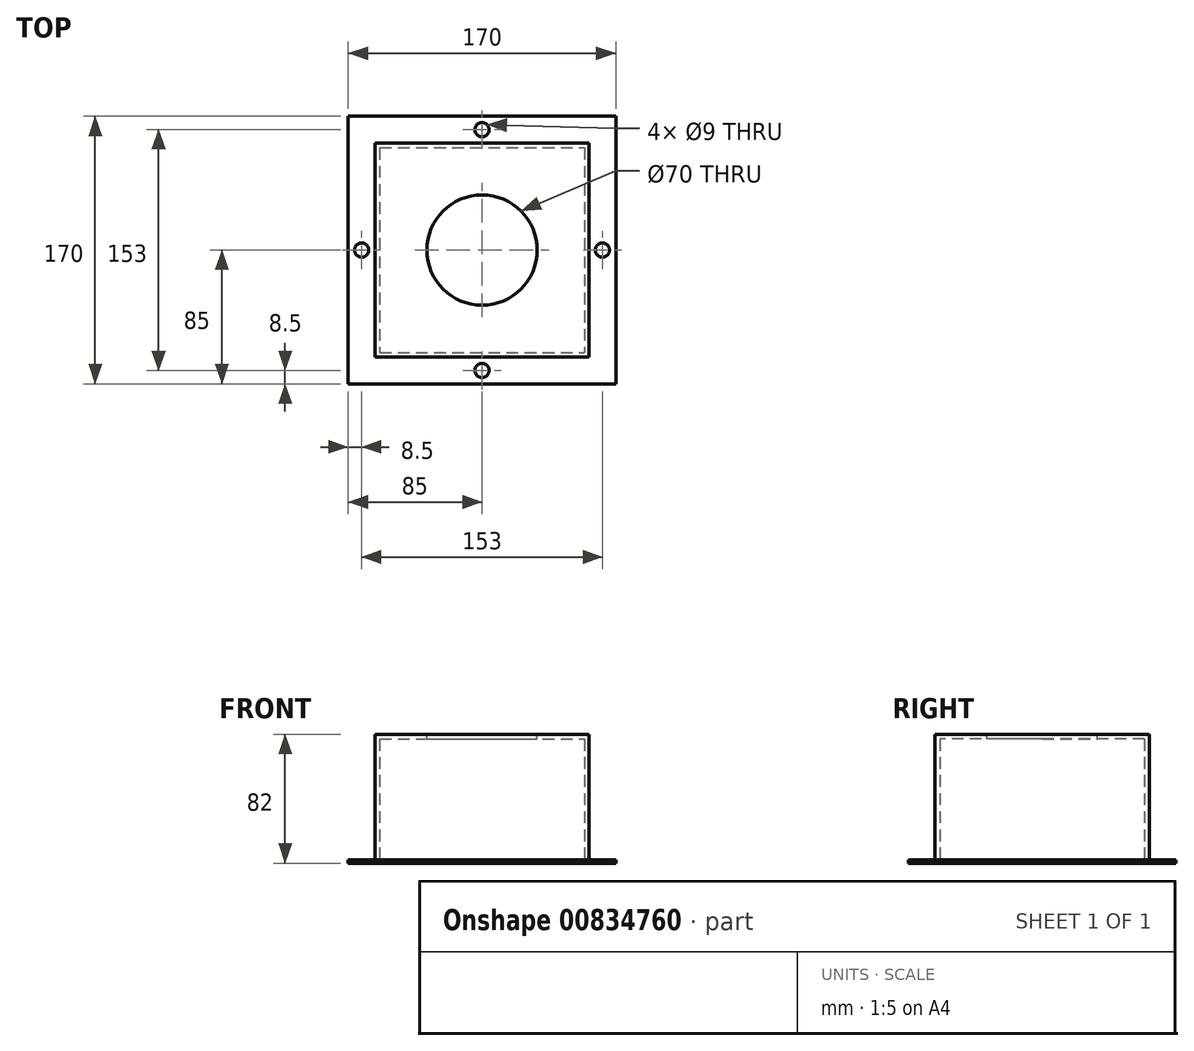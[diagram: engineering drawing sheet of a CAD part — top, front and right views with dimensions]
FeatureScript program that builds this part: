
annotation { "Feature Type Name" : "Feature", "Feature Type Description" : "" }
export const myFeature = defineFeature(function(context is Context, id is Id, definition is map)
    precondition{}
    {
        {
            var Q0;
            Q0=qCreatedBy(makeId("Top.planeOp"),FACE);
            var sketch = newSketch(context, id + "F0", { "sketchPlane" : qUnion([Q0])});
            skLineSegment(sketch, "E0", {"start": v(-85, 85) * mm, "end": v(85, 85) * mm});
            skLineSegment(sketch, "E1", {"start": v(85, 85) * mm, "end": v(85, -85) * mm});
            skLineSegment(sketch, "E2", {"start": v(85, -85) * mm, "end": v(-85, -85) * mm});
            skLineSegment(sketch, "E3", {"start": v(-85, -85) * mm, "end": v(-85, 85) * mm});
            skPoint(sketch, "E4", {"position": v(0, 0) * mm});
            skPoint(sketch, "E4.positionSnap0", {"position": v(-85, 0) * mm});
            skPoint(sketch, "E4.positionSnap1", {"position": v(0, 85) * mm});
            skLineSegment(sketch, "E5.bottom", {"start": v(-65, 65) * mm, "end": v(65, 65) * mm});
            skLineSegment(sketch, "E5.top", {"start": v(-65, -65) * mm, "end": v(65, -65) * mm});
            skLineSegment(sketch, "E5.left", {"start": v(-65, 65) * mm, "end": v(-65, -65) * mm});
            skLineSegment(sketch, "E5.right", {"start": v(65, 65) * mm, "end": v(65, -65) * mm});
            skSolve(sketch);
        }
        {
            var Q0;
            Q0=makeQuery(id+"F0.imprint","IMPRINT",FACE,{"disambiguationData":[TD([[makeQuery(id+"F0.imprint","IMPRINT",EDGE,{"derivedFrom":sQuery(id+"F0.wireOp",EDGE,"E0")}),-1.0]])]});
            extrude(context, id + "F1", {"entities" : qUnion([Q0]), "depth" : 2 * mm, "offsetDistance" : 25 * mm});
        }
        {
            var Q0;
            Q0=makeQuery(id+"F1.opExtrude","CAP_FACE",FACE,{"disambiguationData":[OSD([sQuery(id+"F0.wireOp",EDGE,"E0"),sQuery(id+"F0.wireOp",EDGE,"E1"),sQuery(id+"F0.wireOp",EDGE,"E2"),sQuery(id+"F0.wireOp",EDGE,"E3"),sQuery(id+"F0.wireOp",EDGE,"E5.bottom"),sQuery(id+"F0.wireOp",EDGE,"E5.top"),sQuery(id+"F0.wireOp",EDGE,"E5.left"),sQuery(id+"F0.wireOp",EDGE,"E5.right")])],"isStart":false});
            var sketch = newSketch(context, id + "F2", { "sketchPlane" : qUnion([Q0])});
            skLineSegment(sketch, "E6.bottom", {"start": v(-68, 68) * mm, "end": v(68, 68) * mm});
            skLineSegment(sketch, "E6.top", {"start": v(-68, -68) * mm, "end": v(68, -68) * mm});
            skLineSegment(sketch, "E6.left", {"start": v(-68, 68) * mm, "end": v(-68, -68) * mm});
            skLineSegment(sketch, "E6.right", {"start": v(68, 68) * mm, "end": v(68, -68) * mm});
            skSolve(sketch);
        }
        {
            var Q0;
            Q0 = qSketchRegion(id + "F2", true);
            extrude(context, id + "F3", {"entities" : qUnion([Q0]), "operationType" : NewBodyOperationType.ADD, "depth" : 80 * mm, "offsetDistance" : 25 * mm});
        }
        {
            var Q0;
            Q0=makeQuery(id+"F3.opExtrude","CAP_FACE",FACE,{"disambiguationData":[OSD([sQuery(id+"F2.wireOp",EDGE,"E6.bottom"),sQuery(id+"F2.wireOp",EDGE,"E6.top"),sQuery(id+"F2.wireOp",EDGE,"E6.left"),sQuery(id+"F2.wireOp",EDGE,"E6.right")])],"isStart":true});
            var sketch = newSketch(context, id + "F4", { "sketchPlane" : qUnion([Q0])});
            skLineSegment(sketch, "E7.bottom", {"start": v(-65, 65) * mm, "end": v(65, 65) * mm});
            skLineSegment(sketch, "E7.top", {"start": v(-65, -65) * mm, "end": v(65, -65) * mm});
            skLineSegment(sketch, "E7.left", {"start": v(-65, 65) * mm, "end": v(-65, -65) * mm});
            skLineSegment(sketch, "E7.right", {"start": v(65, 65) * mm, "end": v(65, -65) * mm});
            skSolve(sketch);
        }
        {
            var Q0;
            Q0 = qSketchRegion(id + "F4", true);
            extrude(context, id + "F5", {"entities" : qUnion([Q0]), "operationType" : NewBodyOperationType.REMOVE, "oppositeDirection" : true, "depth" : 77 * mm, "offsetDistance" : 25 * mm});
        }
        {
            var Q0;
            Q0=makeQuery(id+"F3.opExtrude","CAP_FACE",FACE,{"disambiguationData":[OSD([sQuery(id+"F2.wireOp",EDGE,"E6.bottom"),sQuery(id+"F2.wireOp",EDGE,"E6.top"),sQuery(id+"F2.wireOp",EDGE,"E6.left"),sQuery(id+"F2.wireOp",EDGE,"E6.right")])],"isStart":false});
            var sketch = newSketch(context, id + "F6", { "sketchPlane" : qUnion([Q0])});
            skCircle(sketch, "E8", {"center": v(0, 0) * mm, "radius": 35 * mm});
            skSolve(sketch);
        }
        {
            var Q0;
            Q0=makeQuery(id+"F6.imprint","IMPRINT",FACE,{"disambiguationData":[TD([[makeQuery(id+"F6.imprint","IMPRINT",EDGE,{"derivedFrom":sQuery(id+"F6.wireOp",EDGE,"E8")}),1.0]])]});
            extrude(context, id + "F7", {"entities" : qUnion([Q0]), "operationType" : NewBodyOperationType.REMOVE, "endBound" : BoundingType.THROUGH_ALL, "oppositeDirection" : true, "depth" : 25 * mm, "offsetDistance" : 25 * mm});
        }
        {
            var Q0;
            Q0=makeQuery(id+"F1.opExtrude","CAP_FACE",FACE,{"disambiguationData":[OSD([sQuery(id+"F0.wireOp",EDGE,"E0"),sQuery(id+"F0.wireOp",EDGE,"E1"),sQuery(id+"F0.wireOp",EDGE,"E2"),sQuery(id+"F0.wireOp",EDGE,"E3"),sQuery(id+"F0.wireOp",EDGE,"E5.bottom"),sQuery(id+"F0.wireOp",EDGE,"E5.top"),sQuery(id+"F0.wireOp",EDGE,"E5.left"),sQuery(id+"F0.wireOp",EDGE,"E5.right")])],"isStart":false});
            var sketch = newSketch(context, id + "F8", { "sketchPlane" : qUnion([Q0])});
            skLineSegment(sketch, "E9", {"start": v(-85, 0) * mm, "end": v(-68, 0) * mm, "construction": true});
            skLineSegment(sketch, "E10", {"start": v(0, 85) * mm, "end": v(0, 68) * mm, "construction": true});
            skLineSegment(sketch, "E11", {"start": v(68, 0) * mm, "end": v(85, 0) * mm, "construction": true});
            skLineSegment(sketch, "E12", {"start": v(0, -68) * mm, "end": v(0, -85) * mm, "construction": true});
            skPoint(sketch, "E13", {"position": v(-76.5, 0) * mm});
            skPoint(sketch, "E14", {"position": v(0, 76.5) * mm});
            skPoint(sketch, "E15", {"position": v(76.5, 0) * mm});
            skPoint(sketch, "E16", {"position": v(0, -76.5) * mm});
            skCircle(sketch, "E17", {"center": v(0, 76.5) * mm, "radius": 4.5 * mm});
            skCircle(sketch, "E18", {"center": v(-76.5, 0) * mm, "radius": 4.5 * mm});
            skCircle(sketch, "E19", {"center": v(76.5, 0) * mm, "radius": 4.5 * mm});
            skCircle(sketch, "E20", {"center": v(0, -76.5) * mm, "radius": 4.5 * mm});
            skSolve(sketch);
        }
        {
            var Q0;
            Q0 = qSketchRegion(id + "F8", true);
            extrude(context, id + "F9", {"entities" : qUnion([Q0]), "operationType" : NewBodyOperationType.REMOVE, "endBound" : BoundingType.THROUGH_ALL, "oppositeDirection" : true, "depth" : 25 * mm, "offsetDistance" : 25 * mm});
        }
    });
